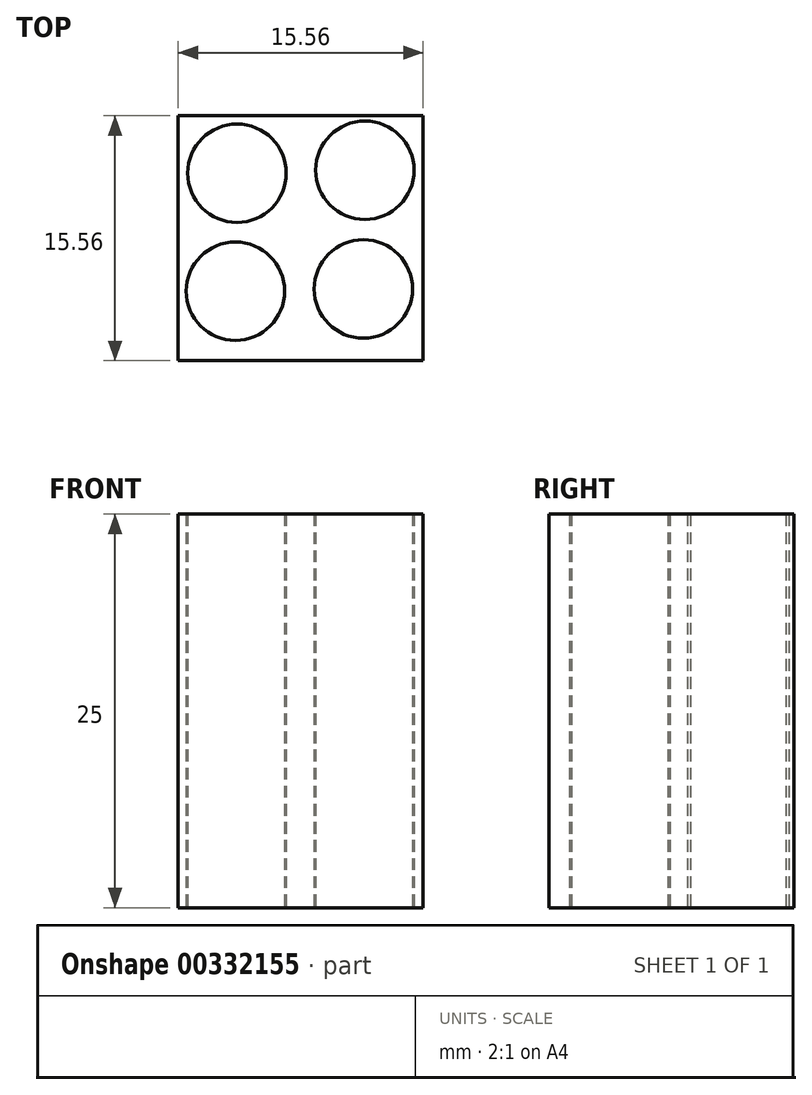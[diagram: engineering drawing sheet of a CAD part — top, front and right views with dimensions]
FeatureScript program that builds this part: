
annotation { "Feature Type Name" : "Feature", "Feature Type Description" : "" }
export const myFeature = defineFeature(function(context is Context, id is Id, definition is map)
    precondition{}
    {
        {
            var Q0;
            Q0=qCreatedBy(makeId("Top.planeOp"),FACE);
            var sketch = newSketch(context, id + "F0", { "sketchPlane" : qUnion([Q0])});
            skLineSegment(sketch, "E0.bottom", {"start": v(-7.7, 6.99) * mm, "end": v(7.86, 6.99) * mm});
            skLineSegment(sketch, "E0.top", {"start": v(-7.7, -8.57) * mm, "end": v(7.86, -8.57) * mm});
            skLineSegment(sketch, "E0.left", {"start": v(-7.7, 6.99) * mm, "end": v(-7.7, -8.57) * mm});
            skLineSegment(sketch, "E0.right", {"start": v(7.86, 6.99) * mm, "end": v(7.86, -8.57) * mm});
            skSolve(sketch);
        }
        {
            var Q0;
            Q0=qCreatedBy(makeId("Top.planeOp"),FACE);
            var sketch = newSketch(context, id + "F1", { "sketchPlane" : qUnion([Q0])});
            skCircle(sketch, "E1", {"center": v(-3.96, 3.34) * mm, "radius": 3.12 * mm});
            skCircle(sketch, "E2", {"center": v(4.16, 3.53) * mm, "radius": 3.12 * mm});
            skCircle(sketch, "E3", {"center": v(-4.07, -4.16) * mm, "radius": 3.12 * mm});
            skCircle(sketch, "E4", {"center": v(4.07, -4.01) * mm, "radius": 3.12 * mm});
            skSolve(sketch);
        }
        {
            var Q0;
            Q0 = qSketchRegion(id + "F0", true);
            var Q1;
            Q1 = qSketchRegion(id + "F1", true);
            extrude(context, id + "F2", {"entities" : qUnion([Q0, Q1]), "depth" : 25 * mm});
        }
    });
